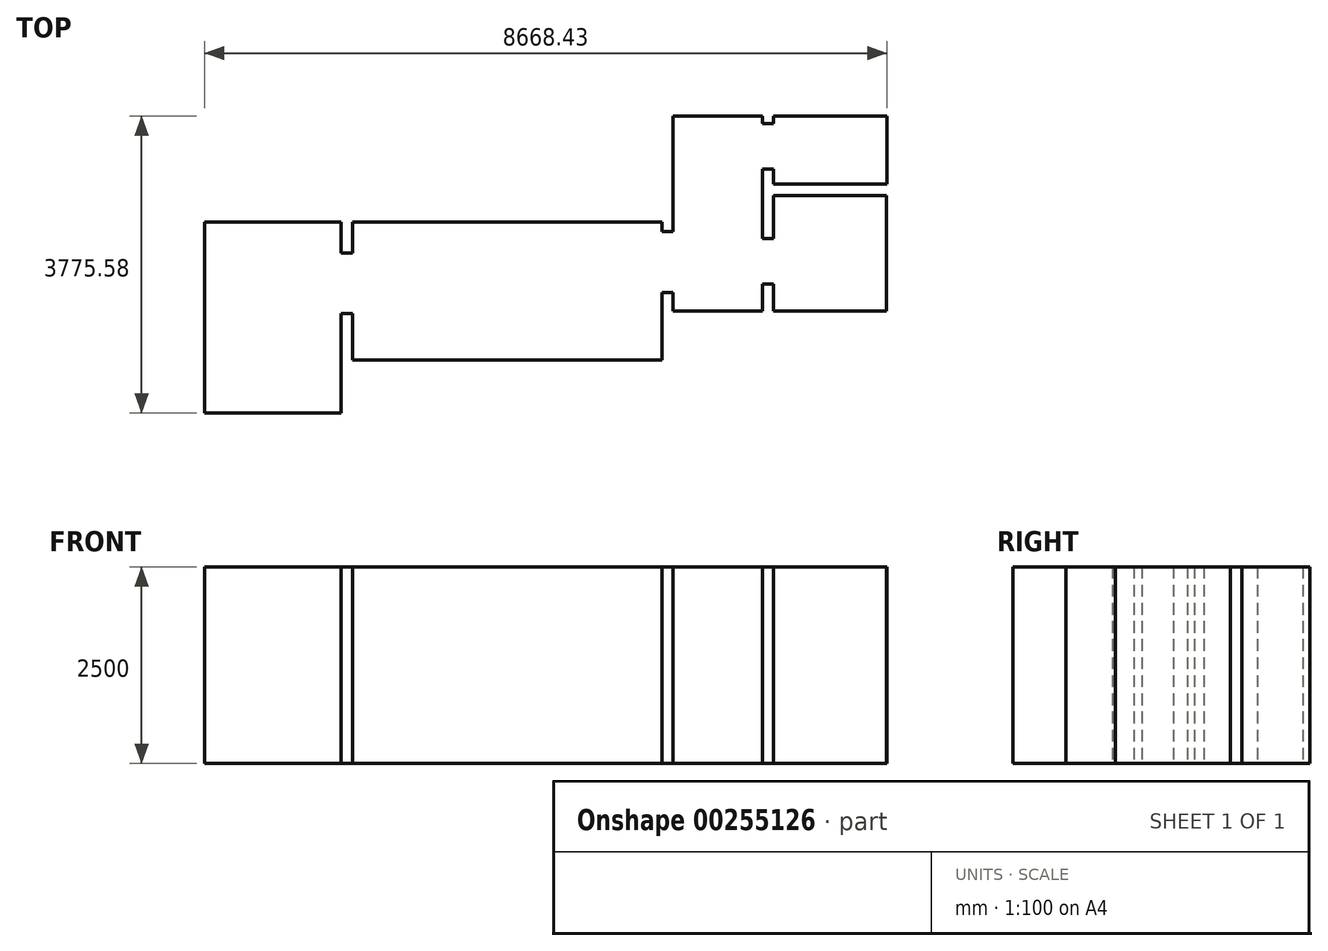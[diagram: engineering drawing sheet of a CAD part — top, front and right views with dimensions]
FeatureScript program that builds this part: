
annotation { "Feature Type Name" : "Feature", "Feature Type Description" : "" }
export const myFeature = defineFeature(function(context is Context, id is Id, definition is map)
    precondition{}
    {
        {
            var Q0;
            Q0=qCreatedBy(makeId("Top.planeOp"),FACE);
            var sketch = newSketch(context, id + "F0", { "sketchPlane" : qUnion([Q0])});
            skLineSegment(sketch, "E0", {"start": v(1798.64, -1271.37) * mm, "end": v(1798.64, -1035.5) * mm});
            skLineSegment(sketch, "E1", {"start": v(1798.64, -1035.5) * mm, "end": v(1654.17, -1035.5) * mm});
            skLineSegment(sketch, "E2", {"start": v(1654.17, -1035.5) * mm, "end": v(1654.17, -1897.42) * mm});
            skLineSegment(sketch, "E3", {"start": v(-2275.52, -144.47) * mm, "end": v(-2275.52, -535.57) * mm});
            skLineSegment(sketch, "E4", {"start": v(-2275.52, -535.57) * mm, "end": v(-2420, -535.57) * mm});
            skLineSegment(sketch, "E5", {"start": v(-2420, -535.57) * mm, "end": v(-2420, -144.47) * mm});
            skLineSegment(sketch, "E6", {"start": v(1798.64, -264.96) * mm, "end": v(1798.64, 1203.95) * mm});
            skLineSegment(sketch, "E7", {"start": v(-2275.52, -1897.42) * mm, "end": v(-2275.52, -1306.1) * mm});
            skLineSegment(sketch, "E8", {"start": v(-2275.52, -1306.1) * mm, "end": v(-2420, -1306.1) * mm});
            skLineSegment(sketch, "E9", {"start": v(-2420, -1306.1) * mm, "end": v(-2420, -2571.63) * mm});
            skLineSegment(sketch, "E10", {"start": v(-2420, -2571.63) * mm, "end": v(-4153.68, -2571.63) * mm});
            skLineSegment(sketch, "E11", {"start": v(2931.07, 1203.95) * mm, "end": v(2931.07, 1109.04) * mm});
            skLineSegment(sketch, "E12", {"start": v(2931.07, 1109.04) * mm, "end": v(3075.54, 1109.04) * mm});
            skLineSegment(sketch, "E13", {"start": v(3075.54, 1109.04) * mm, "end": v(3075.54, 1203.95) * mm});
            skLineSegment(sketch, "E14", {"start": v(2931.07, 531.15) * mm, "end": v(3075.54, 531.15) * mm});
            skLineSegment(sketch, "E15", {"start": v(3075.54, 531.15) * mm, "end": v(3075.54, 337.1) * mm});
            skLineSegment(sketch, "E16", {"start": v(3075.54, 337.1) * mm, "end": v(4514.75, 337.1) * mm});
            skLineSegment(sketch, "E17", {"start": v(2931.07, 531.15) * mm, "end": v(2931.07, -355.45) * mm});
            skLineSegment(sketch, "E18", {"start": v(2931.07, -355.45) * mm, "end": v(3075.54, -355.45) * mm});
            skLineSegment(sketch, "E19", {"start": v(3075.54, -355.45) * mm, "end": v(3075.54, 192.63) * mm});
            skLineSegment(sketch, "E20", {"start": v(3075.54, 192.63) * mm, "end": v(4506.4, 192.63) * mm});
            skLineSegment(sketch, "E21", {"start": v(4514.75, 337.1) * mm, "end": v(4514.75, 1203.95) * mm});
            skLineSegment(sketch, "E22", {"start": v(2931.07, -933.35) * mm, "end": v(3075.54, -933.35) * mm});
            skLineSegment(sketch, "E23", {"start": v(3075.54, -933.35) * mm, "end": v(3075.54, -1271.37) * mm});
            skLineSegment(sketch, "E24", {"start": v(2931.07, -933.35) * mm, "end": v(2931.07, -1271.37) * mm});
            skLineSegment(sketch, "E25", {"start": v(4506.4, -1271.37) * mm, "end": v(4506.4, 192.63) * mm});
            skLineSegment(sketch, "E26", {"start": v(3075.54, -1271.37) * mm, "end": v(4506.4, -1271.37) * mm});
            skLineSegment(sketch, "E27", {"start": v(1654.17, -144.47) * mm, "end": v(1654.17, -265.6) * mm});
            skLineSegment(sketch, "E28", {"start": v(1798.64, -264.96) * mm, "end": v(1654.17, -264.96) * mm});
            skLineSegment(sketch, "E29", {"start": v(-4153.68, -2571.63) * mm, "end": v(-4153.68, -144.47) * mm});
            skLineSegment(sketch, "E30", {"start": v(-4153.68, -144.47) * mm, "end": v(-2420, -144.47) * mm});
            skLineSegment(sketch, "E31", {"start": v(-2275.52, -1897.42) * mm, "end": v(1654.17, -1897.42) * mm});
            skLineSegment(sketch, "E32", {"start": v(1798.64, -1271.37) * mm, "end": v(2931.07, -1271.37) * mm});
            skLineSegment(sketch, "E33", {"start": v(1798.64, 1203.95) * mm, "end": v(2931.07, 1203.95) * mm});
            skLineSegment(sketch, "E34", {"start": v(3075.54, 1203.95) * mm, "end": v(4514.75, 1203.95) * mm});
            skLineSegment(sketch, "E35", {"start": v(-2275.52, -144.47) * mm, "end": v(1654.17, -144.47) * mm});
            skPoint(sketch, "E36", {"position": v(2407.9, 0) * mm});
            skPoint(sketch, "E37", {"position": v(2407.9, 626.05) * mm});
            skPoint(sketch, "E38", {"position": v(2407.9, -626.05) * mm});
            skPoint(sketch, "E39", {"position": v(-650, -1100) * mm});
            skSolve(sketch);
        }
        {
            var Q0;
            Q0=qSketchRegion(id+"F0",true);
            extrude(context, id + "F1", {"entities" : qUnion([Q0]), "offsetDistance" : 25 * mm, "depth" : 2500 * mm});
        }
    });
